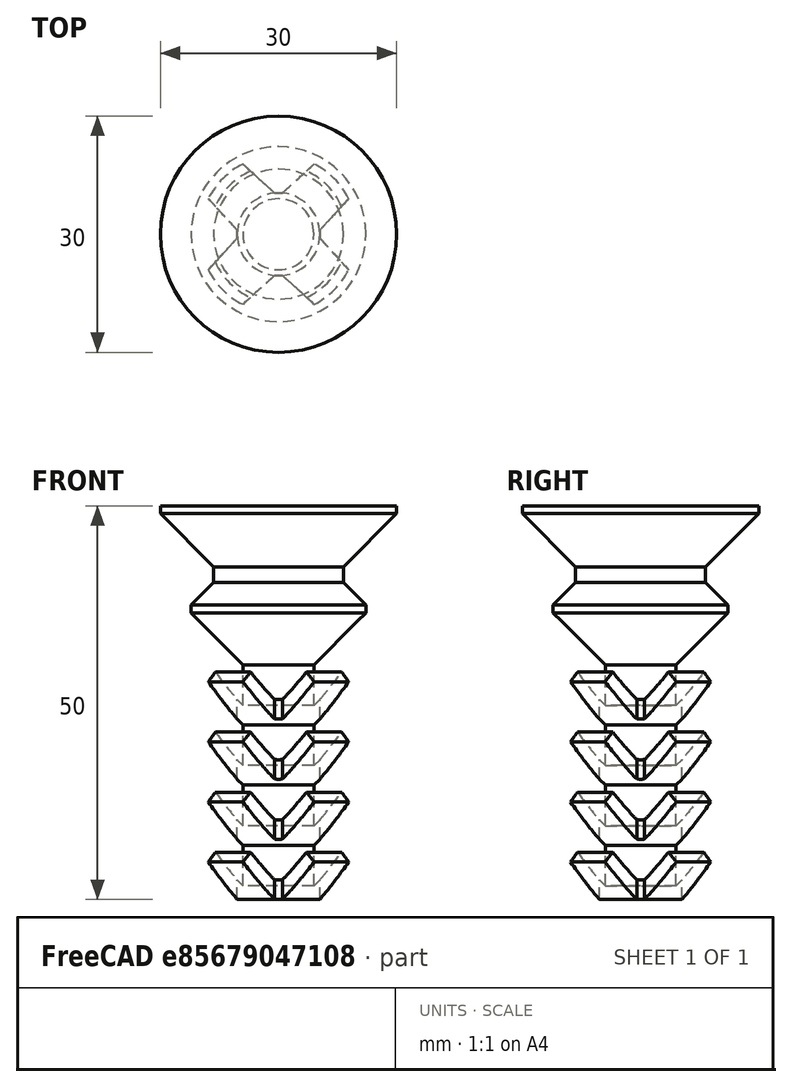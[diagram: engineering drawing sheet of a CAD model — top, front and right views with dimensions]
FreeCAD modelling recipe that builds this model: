
FCSTD DOCUMENT  (FreeCAD 0.19R)
Label: barplug
License: All rights reserved
LicenseURL: http://en.wikipedia.org/wiki/All_rights_reserved
objects: Sketcher::SketchObject×2, PartDesign::Revolution×1, PartDesign::Pocket×1, PartDesign::PolarPattern×1, PartDesign::Body×1, Mesh::Feature×1
note: 8 computed .brp shape members not serialized (recipe doc carries the construction recipe); baked Part::Feature solids carry a one-line shape summary decoded from their .brp

FEATURE [Sketcher::SketchObject] Sketch
  FullyConstrained = false
  MapMode = 5
  Placement = pos=(0,0,0) rot=(1,0,0;1.5708rad)
  Support = -> [XZ_Plane]
  sketch-geometry (27):
    g0: LineSegment StartX=5.25 StartY=0 StartZ=0 EndX=10 EndY=4.75 EndZ=0
    g1: LineSegment StartX=10 StartY=4.75 StartZ=0 EndX=8.76256 EndY=5.98744 EndZ=0
    g2: LineSegment StartX=8.76256 StartY=5.98744 StartZ=0 EndX=4.5 EndY=1.72487 EndZ=0
    g3: LineSegment StartX=4.5 StartY=1.72487 StartZ=0 EndX=4.5 EndY=6.88292 EndZ=0
    g4: LineSegment StartX=4.5 StartY=6.88292 StartZ=0 EndX=10 EndY=12.3829 EndZ=0
    g5: LineSegment StartX=10 StartY=12.3829 StartZ=0 EndX=8.76256 EndY=13.6204 EndZ=0
    g6: LineSegment StartX=8.76256 StartY=13.6204 StartZ=0 EndX=4.5 EndY=9.35779 EndZ=0
    g7: LineSegment StartX=4.5 StartY=9.35779 StartZ=0 EndX=4.5 EndY=14.5158 EndZ=0
    g8: LineSegment StartX=4.5 StartY=14.5158 StartZ=0 EndX=10 EndY=20.0158 EndZ=0
    g9: LineSegment StartX=10 StartY=20.0158 StartZ=0 EndX=8.76256 EndY=21.2533 EndZ=0
    g10: LineSegment StartX=8.76256 StartY=21.2533 StartZ=0 EndX=4.5 EndY=16.9907 EndZ=0
    g11: LineSegment StartX=4.5 StartY=16.9907 StartZ=0 EndX=4.5 EndY=22.1488 EndZ=0
    g12: LineSegment StartX=4.5 StartY=22.1488 StartZ=0 EndX=10 EndY=27.6488 EndZ=0
    g13: LineSegment StartX=10 StartY=27.6488 StartZ=0 EndX=8.76256 EndY=28.8862 EndZ=0
    g14: LineSegment StartX=8.76256 StartY=28.8862 StartZ=0 EndX=4.5 EndY=24.6236 EndZ=0
    g15: LineSegment StartX=4.5 StartY=24.6236 StartZ=0 EndX=4.5 EndY=29.7817 EndZ=0
    g16: LineSegment StartX=4.5 StartY=29.7817 StartZ=0 EndX=10 EndY=35.2817 EndZ=0
    g17: LineSegment StartX=0 StartY=50 StartZ=0 EndX=0 EndY=0 EndZ=0
    g18: LineSegment StartX=10 StartY=60 StartZ=0 EndX=10 EndY=0 EndZ=0
    g19: LineSegment StartX=5.25 StartY=0 StartZ=0 EndX=0 EndY=0 EndZ=0
    g20: LineSegment StartX=10 StartY=35.2817 StartZ=0 EndX=11.1092 EndY=36.3908 EndZ=0
    g21: LineSegment StartX=11.1092 StartY=36.3908 StartZ=0 EndX=11.1092 EndY=37.3908 EndZ=0
    g22: LineSegment StartX=11.1092 StartY=37.3908 StartZ=0 EndX=8.25 EndY=40.25 EndZ=0
    g23: LineSegment StartX=8.25 StartY=40.25 StartZ=0 EndX=8.25 EndY=42.25 EndZ=0
    g24: LineSegment StartX=8.25 StartY=42.25 StartZ=0 EndX=15 EndY=49 EndZ=0
    g25: LineSegment StartX=15 StartY=49 StartZ=0 EndX=15 EndY=50 EndZ=0
    g26: LineSegment StartX=15 StartY=50 StartZ=0 EndX=0 EndY=50 EndZ=0
  constraints (81):
    c: PointOnObject(g0,g-1)
    c: Coincident(g0,g1)
    c: Coincident(g1,g2)
    c: Coincident(g2,g3)
    c: Vertical(g3)
    c: Coincident(g3,g4)
    c: Coincident(g4,g5)
    c: Coincident(g5,g6)
    c: Coincident(g6,g7)
    c: Coincident(g7,g8)
    c: Coincident(g8,g9)
    c: Coincident(g9,g10)
    c: Coincident(g10,g11)
    c: Coincident(g11,g12)
    c: Coincident(g12,g13)
    c: Coincident(g13,g14)
    c: Coincident(g14,g15)
    c: Coincident(g15,g16)
    c: Vertical(g17)
    c: Vertical(g18)
    c: Distance(g18) = 60
    c: PointOnObject(g18,g-1)
    c: PointOnObject(g0,g18)
    c: PointOnObject(g4,g18)
    c: PointOnObject(g8,g18)
    c: PointOnObject(g12,g18)
    c: PointOnObject(g16,g18)
    c: Perpendicular(g4,g5)
    c: Perpendicular(g8,g9)
    c: Perpendicular(g12,g13)
    c: Vertical(g15)
    c: Vertical(g11)
    c: Vertical(g7)
    c: Perpendicular(g9,g10)
    c: Perpendicular(g5,g6)
    c: Perpendicular(g1,g2)
    c: Equal(g2,g6)
    c: Equal(g6,g10)
    c: Equal(g10,g14)
    c: Coincident(g0,g19)
    c: Coincident(g19,g17)
    c: Horizontal(g19)
    c: Coincident(g16,g20)
    c: Coincident(g20,g21)
    c: Coincident(g21,g22)
    c: Coincident(g22,g23)
    c: Vertical(g23)
    c: Coincident(g23,g24)
    c: Coincident(g24,g25)
    c: Coincident(g25,g26)
    c: PointOnObject(g26,g-2)
    c: Horizontal(g26)
    c: Coincident(g17,g26)
    c: Equal(g1,g5)
    c: Equal(g5,g9)
    c: Equal(g9,g13)
    c: Distance(g5) = 1.75
    c: Parallel(g14,g12)
    c: Parallel(g0,g2)
    c: Parallel(g2,g6)
    c: Parallel(g8,g6)
    c: Parallel(g10,g12)
    c: Parallel(g16,g14)
    c: Angle(g22) = 2.35619
    c: Angle(g24) = 0.785398
    c: Vertical(g21)
    c: Vertical(g25)
    c: Angle(g14) = -2.35619
    c: Distance(g21) = 1
    c: Distance(g25) = 1
    c: Equal(g15,g3)
    c: Equal(g3,g7)
    c: Equal(g7,g11)
    c: Distance(g17) = 50
    c: DistanceX(g18) = 10
    c: DistanceX(g22) = 8.25
    c: DistanceX(g3) = 4.5
    c: Distance(g19) = 5.25
    c: DistanceX(g25) = 15
    c: Parallel(g16,g20)
    c: Distance(g23) = 2
FEATURE [PartDesign::Revolution] Revolution
  Angle = 360
  Axis = (0,2e-16,1)
  Base = (0,0,0)
  Placement = pos=(0,0,0) rot=(1,0,0;1.5708rad)
  Profile = -> Sketch
  ReferenceAxis = -> Sketch [V_Axis]
  Reversed = true
FEATURE [Sketcher::SketchObject] Sketch001
  ExternalGeometry = -> [Revolution]
  FullyConstrained = false
  MapMode = 5
  Placement = pos=(0,0,0) rot=(1,0,0;3.14159rad)
  Support = -> [Revolution]
  sketch-geometry (4):
    g0: LineSegment StartX=-20 StartY=22.9651 StartZ=0 EndX=20 EndY=22.9651 EndZ=0
    g1: LineSegment StartX=20 StartY=22.9651 StartZ=0 EndX=0.5 EndY=5.25 EndZ=0
    g2: LineSegment StartX=0.5 StartY=5.25 StartZ=0 EndX=-0.5 EndY=5.25 EndZ=0
    g3: LineSegment StartX=-0.5 StartY=5.25 StartZ=0 EndX=-20 EndY=22.9651 EndZ=0
  constraints (9):
    c: Coincident(g0,g1)
    c: Coincident(g1,g2)
    c: Coincident(g2,g3)
    c: Coincident(g3,g0)
    c: Tangent(g-3,g2)
    c: Symmetric(g0,g0,g-2)
    c: Distance(g2) = 1
    c: Distance(g0) = 40
    c: Symmetric(g1,g2,g-2)
FEATURE [PartDesign::Pocket] Pocket
  BaseFeature = -> Revolution
  Length = 30
  Length2 = 100
  Placement = pos=(0,0,0) rot=(1,0,0;1.5708rad)
  Profile = -> Sketch001
  Type = 0
FEATURE [PartDesign::PolarPattern] PolarPattern
  Angle = 360
  Axis = -> Z_Axis
  BaseFeature = -> Pocket
  Occurrences = 4
  Originals = -> [Pocket]
  Placement = pos=(0,0,0) rot=(1,0,0;1.5708rad)
FEATURE [PartDesign::Body] Body
  Group = -> [Sketch,Revolution,Sketch001,Pocket,PolarPattern]
  Origin = -> Origin
  Tip = -> PolarPattern
FEATURE [Mesh::Feature] Mesh  label="PolarPattern (Meshed)"
